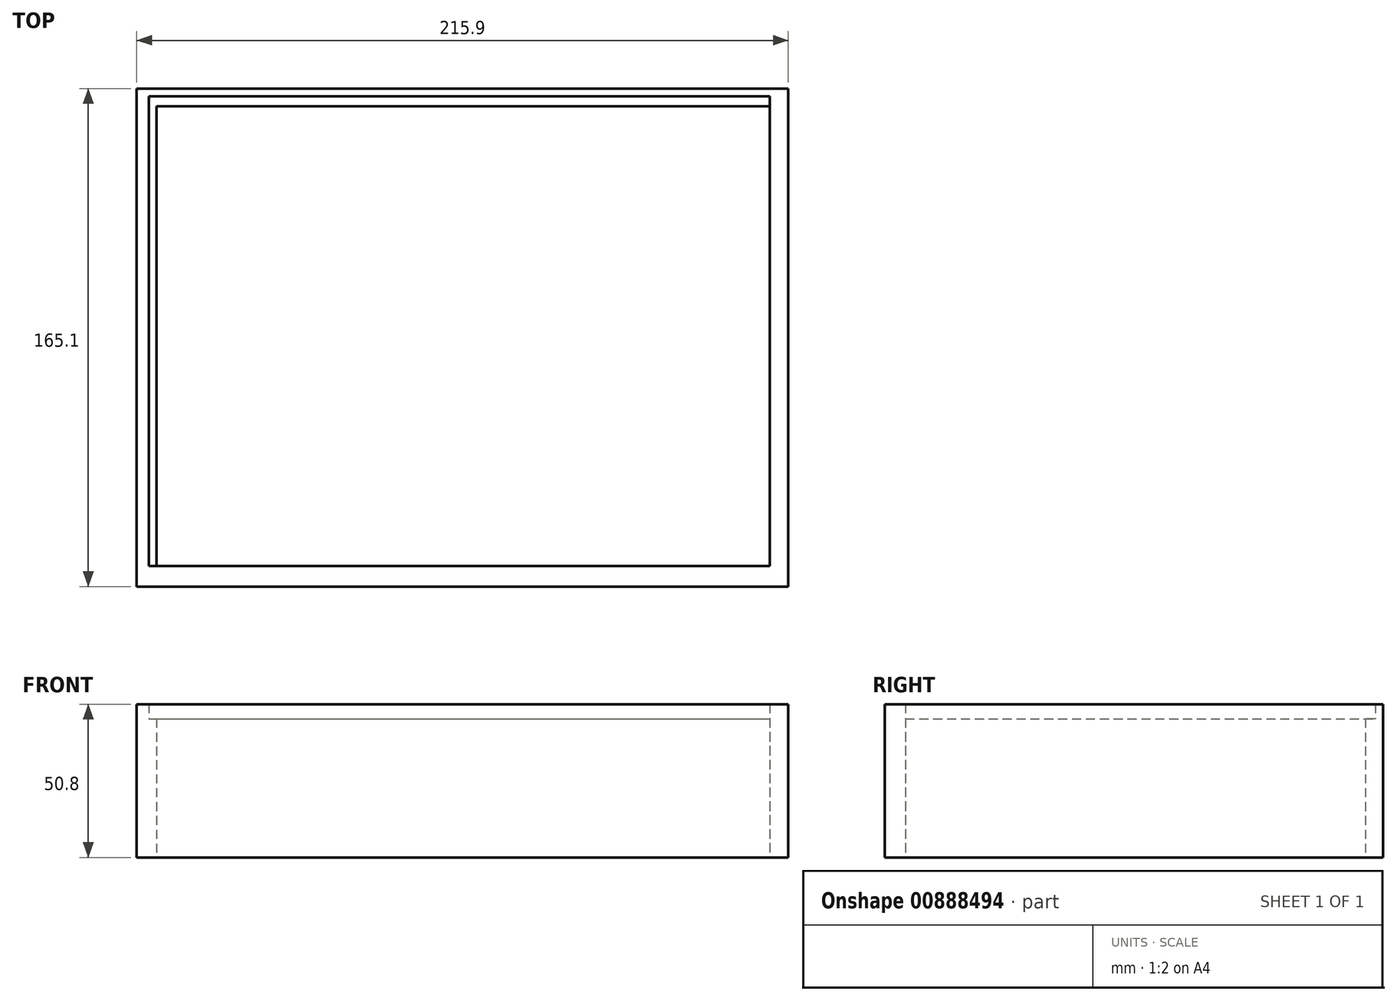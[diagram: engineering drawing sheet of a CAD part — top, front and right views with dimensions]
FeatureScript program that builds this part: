
annotation { "Feature Type Name" : "Feature", "Feature Type Description" : "" }
export const myFeature = defineFeature(function(context is Context, id is Id, definition is map)
    precondition{}
    {
        {
            var Q0;
            Q0=qCreatedBy(makeId("Top.planeOp"),FACE);
            var sketch = newSketch(context, id + "F0", { "sketchPlane" : qUnion([Q0])});
            skLineSegment(sketch, "E0.bottom", {"start": v(0, 0) * mm, "end": v(215.9, 0) * mm});
            skLineSegment(sketch, "E0.top", {"start": v(0, 165.1) * mm, "end": v(215.9, 165.1) * mm});
            skLineSegment(sketch, "E0.left", {"start": v(0, 0) * mm, "end": v(0, 165.1) * mm});
            skLineSegment(sketch, "E0.right", {"start": v(215.9, 0) * mm, "end": v(215.9, 165.1) * mm});
            skSolve(sketch);
        }
        {
            var Q0;
            Q0=makeQuery(id+"F0.imprint","IMPRINT",FACE,{"disambiguationData":[TD([[makeQuery(id+"F0.imprint","IMPRINT",EDGE,{"derivedFrom":sQuery(id+"F0.wireOp",EDGE,"E0.bottom")}),1.0]])]});
            extrude(context, id + "F1", {"entities" : qUnion([Q0]), "depth" : 50.8 * mm});
        }
        {
            var Q0;
            Q0=makeQuery(id+"F1.opExtrude","CAP_FACE",FACE,{"disambiguationData":[OSD([sQuery(id+"F0.wireOp",EDGE,"E0.bottom"),sQuery(id+"F0.wireOp",EDGE,"E0.top"),sQuery(id+"F0.wireOp",EDGE,"E0.left"),sQuery(id+"F0.wireOp",EDGE,"E0.right")])],"isStart":true});
            var sketch = newSketch(context, id + "F2", { "sketchPlane" : qUnion([Q0])});
            skLineSegment(sketch, "E1.bottom", {"start": v(6.54, -6.8) * mm, "end": v(209.74, -6.8) * mm});
            skLineSegment(sketch, "E1.top", {"start": v(6.54, -159.2) * mm, "end": v(209.74, -159.2) * mm});
            skLineSegment(sketch, "E1.left", {"start": v(6.54, -6.8) * mm, "end": v(6.54, -159.2) * mm});
            skLineSegment(sketch, "E1.right", {"start": v(209.74, -6.8) * mm, "end": v(209.74, -159.2) * mm});
            skSolve(sketch);
        }
        {
            var Q0;
            Q0=makeQuery(id+"F2.imprint","IMPRINT",FACE,{"disambiguationData":[TD([[makeQuery(id+"F2.imprint","IMPRINT",EDGE,{"derivedFrom":sQuery(id+"F2.wireOp",EDGE,"E1.bottom")}),-1.0]])]});
            extrude(context, id + "F3", {"entities" : qUnion([Q0]), "operationType" : NewBodyOperationType.REMOVE, "oppositeDirection" : true, "depth" : 50.8 * mm});
        }
        {
            var Q0;
            Q0=makeQuery(id+"F3.boolean.opBoolean","COPY",FACE,{"derivedFrom":makeQuery(id+"F3.opExtrude","SWEPT_FACE",FACE,{"disambiguationData":[OSD([sQuery(id+"F2.wireOp",EDGE,"E1.left")])]})});
            var sketch = newSketch(context, id + "F4", { "sketchPlane" : qUnion([Q0])});
            skLineSegment(sketch, "E2.bottom", {"start": v(6.8, 50.8) * mm, "end": v(159.2, 50.8) * mm});
            skLineSegment(sketch, "E2.top", {"start": v(6.8, 45.96) * mm, "end": v(159.2, 45.96) * mm});
            skLineSegment(sketch, "E2.left", {"start": v(6.8, 50.8) * mm, "end": v(6.8, 45.96) * mm});
            skLineSegment(sketch, "E2.right", {"start": v(159.2, 50.8) * mm, "end": v(159.2, 45.96) * mm});
            skSolve(sketch);
        }
        {
            var Q0;
            Q0=makeQuery(id+"F4.imprint","IMPRINT",FACE,{"disambiguationData":[TD([[makeQuery(id+"F4.imprint","IMPRINT",EDGE,{"derivedFrom":sQuery(id+"F4.wireOp",EDGE,"E2.bottom")}),-1.0]])]});
            extrude(context, id + "F5", {"entities" : qUnion([Q0]), "operationType" : NewBodyOperationType.REMOVE, "oppositeDirection" : true, "depth" : 2.54 * mm});
        }
        {
            var Q0;
            Q0=makeQuery(id+"F5.boolean.opBoolean","MERGE",FACE,{"derivedFrom":[makeQuery(id+"F3.boolean.opBoolean","COPY",FACE,{"derivedFrom":makeQuery(id+"F3.opExtrude","SWEPT_FACE",FACE,{"disambiguationData":[OSD([sQuery(id+"F2.wireOp",EDGE,"E1.top")])]})}),makeQuery(id+"F5.opExtrude","SWEPT_FACE",FACE,{"disambiguationData":[OSD([sQuery(id+"F4.wireOp",EDGE,"E2.right")])]})]});
            var sketch = newSketch(context, id + "F6", { "sketchPlane" : qUnion([Q0])});
            skLineSegment(sketch, "E3.bottom", {"start": v(4, 45.96) * mm, "end": v(209.74, 45.96) * mm});
            skLineSegment(sketch, "E3.top", {"start": v(4, 50.8) * mm, "end": v(209.74, 50.8) * mm});
            skLineSegment(sketch, "E3.left", {"start": v(4, 45.96) * mm, "end": v(4, 50.8) * mm});
            skLineSegment(sketch, "E3.right", {"start": v(209.74, 45.96) * mm, "end": v(209.74, 50.8) * mm});
            skSolve(sketch);
        }
        {
            var Q0;
            Q0=qSketchRegion(id+"F6",true);
            extrude(context, id + "F7", {"entities" : qUnion([Q0]), "operationType" : NewBodyOperationType.REMOVE, "oppositeDirection" : true, "depth" : 3.3 * mm});
        }
    });
